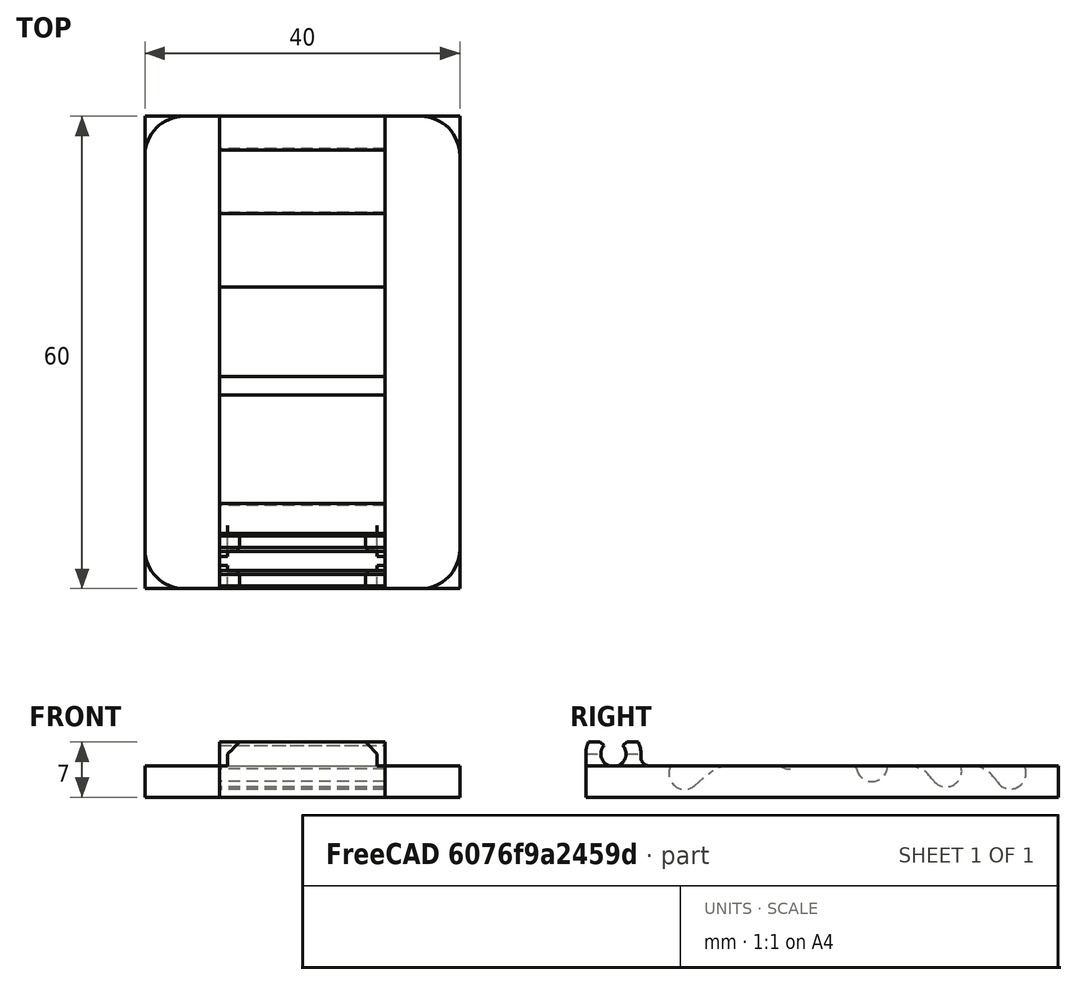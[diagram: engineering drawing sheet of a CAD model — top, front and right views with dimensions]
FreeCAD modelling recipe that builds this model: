
FCSTD DOCUMENT  (FreeCAD 0.14R3700 (Git))
Label: Phone_stand_flippable_base
License: CC-BY 3.0
LicenseURL: http://creativecommons.org/licenses/by/3.0/
objects: Sketcher::SketchObject×3, PartDesign::Pad×2, PartDesign::Pocket×1, PartDesign::Fillet×1, Mesh::Feature×1
note: 10 computed .brp shape members not serialized (recipe doc carries the construction recipe); baked Part::Feature solids carry a one-line shape summary decoded from their .brp

FEATURE [Sketcher::SketchObject] Sketch  label="X-Section"
  Placement = pos=(0,0,0) rot=(0.57735,0.57735,0.57735;2.0944rad)
  sketch-geometry (46):
    g0: LineSegment StartX=0 StartY=0 StartZ=0 EndX=60 EndY=0 EndZ=0
    g1: LineSegment StartX=60 StartY=0 StartZ=0 EndX=60 EndY=4 EndZ=0
    g2: LineSegment StartX=7 StartY=5 StartZ=0 EndX=7 EndY=5.5 EndZ=0
    g3: LineSegment StartX=0 StartY=0 StartZ=0 EndX=0 EndY=5.5 EndZ=0
    g4: ArcOfCircle CenterX=3.5 CenterY=5.5 CenterZ=0 NormalX=0 NormalY=0 NormalZ=1 Radius=1.6 StartAngle=2.41886 EndAngle=7.00592
    g5: LineSegment StartX=4.7 StartY=6.5583 StartZ=0 EndX=5.20084 EndY=7 EndZ=0
    g6: LineSegment StartX=2.3 StartY=6.5583 StartZ=0 EndX=1.79916 EndY=7 EndZ=0
    g7: ArcOfCircle CenterX=3.5 CenterY=5.5 CenterZ=0 NormalX=0 NormalY=0 NormalZ=1 Radius=3.5 StartAngle=0 EndAngle=0.442911
    g8: ArcOfCircle CenterX=3.5 CenterY=5.5 CenterZ=0 NormalX=0 NormalY=0 NormalZ=1 Radius=3.5 StartAngle=2.69868 EndAngle=3.14159
    g9: LineSegment [constr] StartX=3.5 StartY=5.5 StartZ=0 EndX=7 EndY=5.5 EndZ=0
    g10: LineSegment [constr] StartX=3.5 StartY=5.5 StartZ=0 EndX=0 EndY=5.5 EndZ=0
    g11: LineSegment StartX=8 StartY=4 StartZ=0 EndX=10.8058 EndY=4 EndZ=0
    g12: LineSegment [constr] StartX=3.5 StartY=5.5 StartZ=0 EndX=25.7753 EndY=44.6 EndZ=0
    g13: LineSegment [constr] StartX=25.7753 StartY=44.6 StartZ=0 EndX=25.7753 EndY=5.6 EndZ=0
    g14: LineSegment [constr] StartX=3.5 StartY=5.5 StartZ=0 EndX=35.3198 EndY=37.3198 EndZ=0
    g15: LineSegment [constr] StartX=35.3198 StartY=37.3198 StartZ=0 EndX=53.9286 EndY=3.0457 EndZ=0
    g16: LineSegment [constr] StartX=3.5 StartY=5.5 StartZ=0 EndX=42.4711 EndY=28 EndZ=0
    g17: LineSegment [constr] StartX=42.4711 StartY=28 StartZ=0 EndX=12.5379 EndY=3 EndZ=0
    g18: LineSegment [constr] StartX=2.3 StartY=6.5583 StartZ=0 EndX=4.7 EndY=6.5583 EndZ=0
    g19: ArcOfCircle CenterX=12.5379 CenterY=3 CenterZ=0 NormalX=0 NormalY=0 NormalZ=1 Radius=2 StartAngle=2.61799 EndAngle=5.40822
    g20: LineSegment StartX=18.3059 StartY=4 StartZ=0 EndX=24.5753 EndY=4 EndZ=0
    g21: ArcOfCircle CenterX=25.7753 CenterY=5.6 CenterZ=0 NormalX=0 NormalY=0 NormalZ=1 Radius=2 StartAngle=4.06889 EndAngle=5.35589
    g22: LineSegment [constr] StartX=12.5379 StartY=3 StartZ=0 EndX=12.5379 EndY=4 EndZ=0
    g23: ArcOfCircle CenterX=53.9286 CenterY=3.0457 CenterZ=0 NormalX=0 NormalY=0 NormalZ=1 Radius=2 StartAngle=3.67401 EndAngle=6.78059
    g24: LineSegment StartX=55.6862 StartY=4 StartZ=0 EndX=60 EndY=4 EndZ=0
    g25: ArcOfCircle CenterX=48.7591 CenterY=0 CenterZ=0 NormalX=0 NormalY=0 NormalZ=1 Radius=4 StartAngle=0.532416 EndAngle=1.5708
    g26: LineSegment [constr] StartX=12.5379 StartY=3 StartZ=0 EndX=13.8199 EndY=1.46496 EndZ=0
    g27: LineSegment StartX=13.8199 StartY=1.46496 StartZ=0 EndX=15.7418 EndY=3.07007 EndZ=0
    g28: ArcOfCircle CenterX=18.3059 CenterY=0 CenterZ=0 NormalX=0 NormalY=0 NormalZ=1 Radius=4 StartAngle=1.5708 EndAngle=2.26663
    g29: LineSegment [constr] StartX=3.5 StartY=5.5 StartZ=0 EndX=32.4254 EndY=39.972 EndZ=0
    g30: LineSegment [constr] StartX=32.4254 StartY=39.972 StartZ=0 EndX=45.7449 EndY=3.31695 EndZ=0
    g31: ArcOfCircle CenterX=45.7449 CenterY=3.31695 CenterZ=0 NormalX=0 NormalY=0 NormalZ=1 Radius=2 StartAngle=3.72734 EndAngle=6.63172
    g32: LineSegment StartX=48.7591 StartY=4 StartZ=0 EndX=47.6246 EndY=4 EndZ=0
    g33: ArcOfCircle CenterX=40.7451 CenterY=0 CenterZ=0 NormalX=0 NormalY=0 NormalZ=1 Radius=4 StartAngle=0.585751 EndAngle=1.5708
    g34: LineSegment StartX=26.9753 StartY=4 StartZ=0 EndX=33.9377 EndY=4 EndZ=0
    g35: LineSegment [constr] StartX=3.5 StartY=5.5 StartZ=0 EndX=29.3109 EndY=42.3618 EndZ=0
    g36: LineSegment [constr] StartX=29.3109 StartY=42.3618 StartZ=0 EndX=36.3373 EndY=4 EndZ=0
    g37: ArcOfCircle CenterX=36.3373 CenterY=4 CenterZ=0 NormalX=0 NormalY=0 NormalZ=1 Radius=2 StartAngle=3.32274 EndAngle=6.28319
    g38: LineSegment [constr] StartX=45.7449 StartY=3.31695 StartZ=0 EndX=47.6246 EndY=4 EndZ=0
    g39: LineSegment StartX=38.3373 StartY=4 StartZ=0 EndX=40.7451 EndY=4 EndZ=0
    g40: ArcOfCircle CenterX=33.9377 CenterY=3.56049 CenterZ=0 NormalX=0 NormalY=0 NormalZ=1 Radius=0.439506 StartAngle=0.181151 EndAngle=1.5708
    g41: LineSegment [constr] StartX=34.37 StartY=3.63968 StartZ=0 EndX=36.3373 EndY=4 EndZ=0
    g42: LineSegment [constr] StartX=55.6862 StartY=4 StartZ=0 EndX=53.9286 EndY=3.0457 EndZ=0
    g43: LineSegment StartX=0.337722 StartY=7 StartZ=0 EndX=1.79916 EndY=7 EndZ=0
    g44: LineSegment StartX=5.20084 StartY=7 StartZ=0 EndX=6.66228 EndY=7 EndZ=0
    g45: ArcOfCircle CenterX=8 CenterY=5 CenterZ=0 NormalX=0 NormalY=0 NormalZ=1 Radius=1 StartAngle=3.14159 EndAngle=4.71239
  constraints (136):
    c: Horizontal(g0)
    c: Coincident(g1,g0)
    c: Vertical(g1)
    c: Vertical(g2)
    c: Vertical(g3)
    c: Coincident(g0,g3)
    c: DistanceY(g1) = 4
    c: Coincident(g0,g-1)
    c: Coincident(g5,g4)
    c: Coincident(g6,g4)
    c: PointOnObject(g4,g5)
    c: PointOnObject(g4,g6)
    c: Coincident(g7,g4)
    c: Coincident(g8,g4)
    c: Coincident(g8,g3)
    c: Coincident(g2,g7)
    c: Coincident(g9,g4)
    c: Coincident(g9,g2)
    c: Horizontal(g9)
    c: Coincident(g10,g4)
    c: Coincident(g10,g3)
    c: Horizontal(g10)
    c: Radius(g4) = 1.6
    c: DistanceX(g4,g4) = -1.2
    c: Horizontal(g11)
    c: PointOnObject(g1,g11)
    c: Coincident(g12,g4)
    c: Coincident(g13,g12)
    c: Distance(g12) = 45
    c: Distance(g13) = 39
    c: Coincident(g14,g4)
    c: Equal(g14,g12)
    c: Coincident(g15,g14)
    c: Equal(g15,g13)
    c: Angle(g11,g14) = 0.785398
    c: Coincident(g16,g4)
    c: Coincident(g17,g16)
    c: Equal(g12,g16)
    c: Equal(g13,g17)
    c: Angle(g11,g16) = 0.523599
    c: Angle(g11,g4) = 0.261799
    c: Radius(g7) = 3.5
    c: Radius(g8) = 3.5
    c: Coincident(g18,g4)
    c: Coincident(g18,g4)
    c: Horizontal(g18)
    c: Horizontal(g20)
    c: PointOnObject(g1,g20)
    c: Coincident(g11,g19)
    c: Coincident(g17,g19)
    c: Radius(g21) = 2
    c: Coincident(g22,g17)
    c: Vertical(g22)
    c: PointOnObject(g22,g11)
    c: DistanceY(g22) = 1
    c: Coincident(g13,g21)
    c: Coincident(g24,g23)
    c: Coincident(g24,g1)
    c: Horizontal(g24)
    c: Radius(g23) = 2
    c: DistanceX(g0) = 60
    c: Coincident(g26,g17)
    c: Angle(g26,g17) = 1.5708
    c: Coincident(g19,g26)
    c: Radius(g19) = 2
    c: Coincident(g27,g19)
    c: Tangent(g27,g19)
    c: Coincident(g28,g27)
    c: Coincident(g28,g20)
    c: Tangent(g28,g27)
    c: Tangent(g28,g20)
    c: PointOnObject(g28,g0)
    c: PointOnObject(g25,g0)
    c: Coincident(g29,g4)
    c: Equal(g29,g12)
    c: Coincident(g30,g29)
    c: Equal(g30,g13)
    c: Angle(g11,g29) = 0.872665
    c: Radius(g31) = 2
    c: Coincident(g32,g25)
    c: Horizontal(g32)
    c: Coincident(g34,g21)
    c: Horizontal(g34)
    c: PointOnObject(g1,g34)
    c: Tangent(g34,g33)
    c: Coincident(g33,g31)
    c: Tangent(g31,g33)
    c: PointOnObject(g1,g32)
    c: Tangent(g25,g32)
    c: Coincident(g35,g4)
    c: Equal(g35,g12)
    c: Coincident(g36,g35)
    c: Equal(g36,g13)
    c: Angle(g11,g35) = 0.959931
    c: Radius(g37) = 2
    c: Coincident(g38,g31)
    c: Horizontal(g39)
    c: Tangent(g39,g33)
    c: Coincident(g40,g34)
    c: Tangent(g40,g34)
    c: Tangent(g40,g37)
    c: Coincident(g20,g21)
    c: DistanceY(g13,g21) = -1.6
    c: Coincident(g37,g36)
    c: Coincident(g37,g40)
    c: PointOnObject(g36,g34)
    c: Coincident(g37,g39)
    c: Coincident(g41,g37)
    c: Coincident(g41,g36)
    c: Perpendicular(g36,g41)
    c: Vertical(g13)
    c: Coincident(g38,g31)
    c: Coincident(g39,g33)
    c: Perpendicular(g30,g38)
    c: Coincident(g30,g31)
    c: PointOnObject(g31,g39)
    c: Coincident(g32,g31)
    c: Coincident(g42,g23)
    c: Coincident(g42,g23)
    c: Perpendicular(g15,g42)
    c: Coincident(g15,g23)
    c: PointOnObject(g33,g0)
    c: Coincident(g23,g25)
    c: Tangent(g25,g23)
    c: Horizontal(g43)
    c: Coincident(g6,g43)
    c: Coincident(g8,g43)
    c: Horizontal(g44)
    c: Coincident(g7,g44)
    c: Coincident(g5,g44)
    c: PointOnObject(g5,g43)
    c: Tangent(g2,g45)
    c: Tangent(g11,g45)
    c: Radius(g45) = 1
    c: DistanceY(g2,g11) = -1.5
    c: DistanceY(g8,g11) = -3
FEATURE [PartDesign::Pad] Pad
  Length = 21
  Length2 = 100
  Midplane = true
  Placement = pos=(0,0,0) rot=(0.57735,0.57735,0.57735;2.0944rad)
  Sketch = -> Sketch
  Type = 0
FEATURE [Sketcher::SketchObject] Sketch002  label="Side-Pad"
  ExternalGeometry = -> [Pad]
  Placement = pos=(0,0,4) rot=(0,0,-1;1.5708rad)
  Support = -> Pad [Face20]
  sketch-geometry (8):
    g0: LineSegment StartX=-60 StartY=10.5 StartZ=0 EndX=0 EndY=10.5 EndZ=0
    g1: LineSegment StartX=0 StartY=10.5 StartZ=0 EndX=0 EndY=20 EndZ=0
    g2: LineSegment StartX=0 StartY=20 StartZ=0 EndX=-60 EndY=20 EndZ=0
    g3: LineSegment StartX=-60 StartY=20 StartZ=0 EndX=-60 EndY=10.5 EndZ=0
    g4: LineSegment StartX=-60 StartY=-20 StartZ=0 EndX=0 EndY=-20 EndZ=0
    g5: LineSegment StartX=0 StartY=-20 StartZ=0 EndX=0 EndY=-10.5 EndZ=0
    g6: LineSegment StartX=0 StartY=-10.5 StartZ=0 EndX=-60 EndY=-10.5 EndZ=0
    g7: LineSegment StartX=-60 StartY=-10.5 StartZ=0 EndX=-60 EndY=-20 EndZ=0
  constraints (22):
    c: Coincident(g0,g1)
    c: Coincident(g1,g2)
    c: Coincident(g2,g3)
    c: Coincident(g3,g0)
    c: Horizontal(g0)
    c: Horizontal(g2)
    c: Vertical(g1)
    c: Vertical(g3)
    c: PointOnObject(g1,g-2)
    c: Coincident(g4,g5)
    c: Coincident(g5,g6)
    c: Coincident(g6,g7)
    c: Coincident(g7,g4)
    c: Horizontal(g4)
    c: Horizontal(g6)
    c: Vertical(g5)
    c: Vertical(g7)
    c: PointOnObject(g5,g-2)
    c: Equal(g3,g7)
    c: DistanceY(g2,g4) = -40
    c: Coincident(g0,g-3)
    c: Coincident(g6,g-3)
FEATURE [PartDesign::Pad] Pad001
  Length = 4
  Length2 = 100
  Placement = pos=(0,0,0) rot=(0.57735,0.57735,0.57735;2.0944rad)
  Reversed = true
  Sketch = -> Sketch002
  Type = 0
FEATURE [Sketcher::SketchObject] Sketch003  label="Hinge-Pocket"
  ExternalGeometry = -> [Pad001]
  Placement = pos=(0,0,0) rot=(-0.57735,-0.57735,0.57735;4.18879rad)
  Support = -> Pad001 [Face3]
  sketch-geometry (10):
    g0: LineSegment StartX=-7 StartY=10.5 StartZ=0 EndX=-4 EndY=10.5 EndZ=0
    g1: LineSegment StartX=-4 StartY=10.5 StartZ=0 EndX=-4 EndY=9.5 EndZ=0
    g2: LineSegment StartX=-4 StartY=9.5 StartZ=0 EndX=-5.5 EndY=9.5 EndZ=0
    g3: LineSegment StartX=-5.5 StartY=9.5 StartZ=0 EndX=-7 EndY=8 EndZ=0
    g4: LineSegment StartX=-7 StartY=8 StartZ=0 EndX=-7 EndY=10.5 EndZ=0
    g5: LineSegment StartX=-7 StartY=-10.5 StartZ=0 EndX=-4 EndY=-10.5 EndZ=0
    g6: LineSegment StartX=-4 StartY=-10.5 StartZ=0 EndX=-4 EndY=-9.5 EndZ=0
    g7: LineSegment StartX=-4 StartY=-9.5 StartZ=0 EndX=-5.5 EndY=-9.5 EndZ=0
    g8: LineSegment StartX=-7 StartY=-10.5 StartZ=0 EndX=-7 EndY=-8 EndZ=0
    g9: LineSegment StartX=-7 StartY=-8 StartZ=0 EndX=-5.5 EndY=-9.5 EndZ=0
  constraints (28):
    c: Horizontal(g0)
    c: Coincident(g1,g0)
    c: Vertical(g1)
    c: Coincident(g2,g1)
    c: Horizontal(g2)
    c: Coincident(g3,g2)
    c: Vertical(g4)
    c: Coincident(g4,g3)
    c: Coincident(g4,g0)
    c: Angle(g3,g4) = 0.785398
    c: Horizontal(g5)
    c: Coincident(g6,g5)
    c: Vertical(g6)
    c: Coincident(g7,g6)
    c: Horizontal(g7)
    c: Coincident(g8,g5)
    c: Vertical(g8)
    c: Coincident(g9,g8)
    c: Coincident(g9,g7)
    c: Angle(g8,g9) = 0.785398
    c: Equal(g7,g2)
    c: Equal(g1,g6)
    c: DistanceY(g1,g6) = -19
    c: DistanceX(g2) = -1.5
    c: Coincident(g5,g-4)
    c: Coincident(g-3,g0)
    c: Coincident(g0,g-5)
    c: Coincident(g5,g-5)
FEATURE [PartDesign::Pocket] Pocket
  Length = 5
  Placement = pos=(0,0,0) rot=(0.57735,0.57735,0.57735;2.0944rad)
  Sketch = -> Sketch003
  Type = 1
FEATURE [PartDesign::Fillet] Fillet
  Base = -> Pocket [Edge69,Edge100,Edge44,Edge36]
  Placement = pos=(0,0,0) rot=(0.57735,0.57735,0.57735;2.0944rad)
  Radius = 5
FEATURE [Mesh::Feature] Mesh  label="Fillet (Meshed)"
